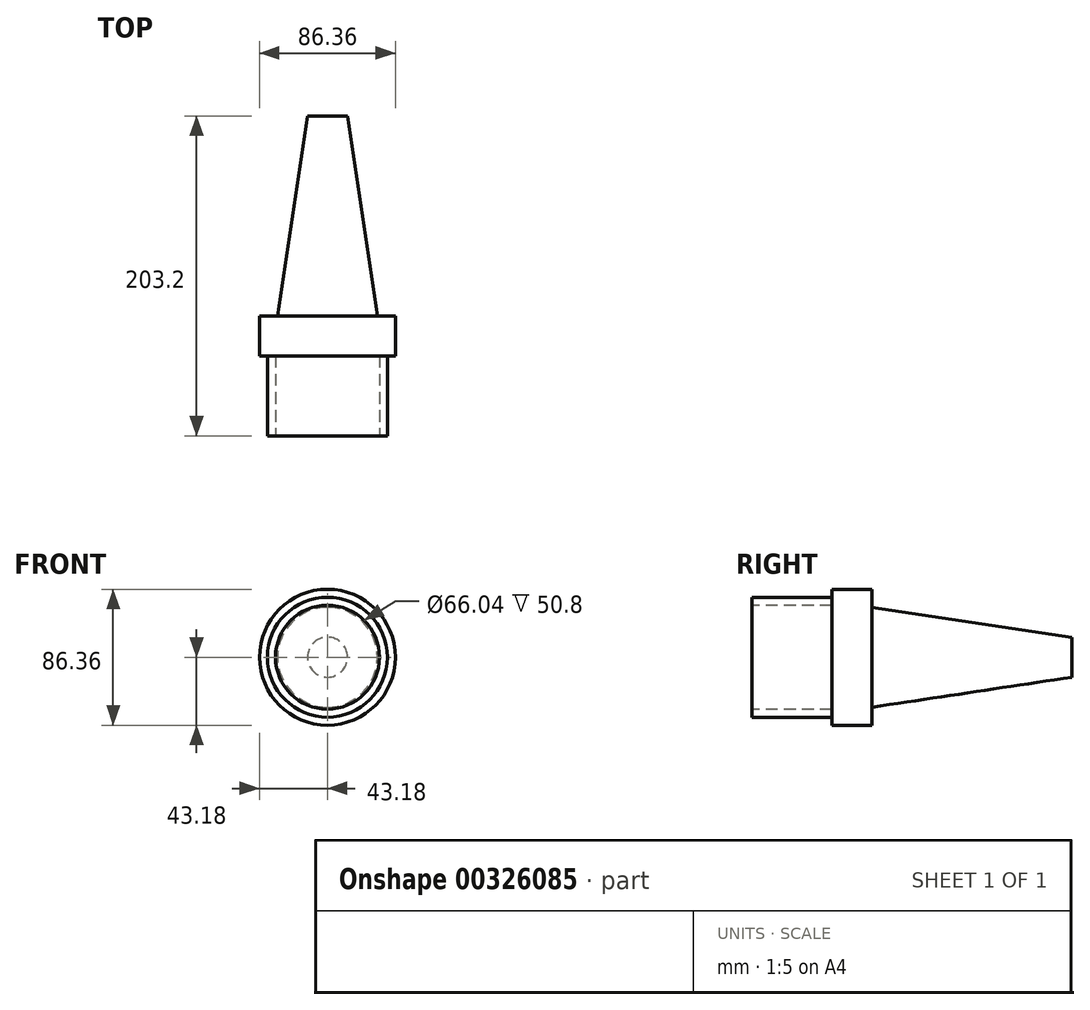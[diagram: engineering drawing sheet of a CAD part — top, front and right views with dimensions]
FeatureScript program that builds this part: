
annotation { "Feature Type Name" : "Feature", "Feature Type Description" : "" }
export const myFeature = defineFeature(function(context is Context, id is Id, definition is map)
    precondition{}
    {
        {
            var Q0;
            Q0=qCreatedBy(makeId("Front.planeOp"),FACE);
            var sketch = newSketch(context, id + "F0", { "sketchPlane" : qUnion([Q0])});
            skCircle(sketch, "E0", {"center": v(0, 0) * mm, "radius": 38.1 * mm});
            skSolve(sketch);
        }
        {
            var Q0;
            Q0 = qSketchRegion(id + "F0", true);
            extrude(context, id + "F1", {"entities" : qUnion([Q0]), "depth" : 76.2 * mm});
        }
        {
            var Q0;
            Q0=makeQuery(id+"F1.opExtrude","CAP_FACE",FACE,{"disambiguationData":[OSD([sQuery(id+"F0.wireOp",EDGE,"E0")])],"isStart":false});
            var sketch = newSketch(context, id + "F2", { "sketchPlane" : qUnion([Q0])});
            skCircle(sketch, "E1", {"center": v(0, 0) * mm, "radius": 33.02 * mm});
            skSolve(sketch);
        }
        {
            var Q0;
            Q0 = qSketchRegion(id + "F2", true);
            extrude(context, id + "F3", {"entities" : qUnion([Q0]), "operationType" : NewBodyOperationType.REMOVE, "oppositeDirection" : true, "depth" : 69.85 * mm});
        }
        {
            var Q0;
            Q0=makeQuery(id+"F1.opExtrude","CAP_FACE",FACE,{"disambiguationData":[OSD([sQuery(id+"F0.wireOp",EDGE,"E0")])],"isStart":true});
            var sketch = newSketch(context, id + "F4", { "sketchPlane" : qUnion([Q0])});
            skCircle(sketch, "E2", {"center": v(0, 0) * mm, "radius": 31.75 * mm});
            skSolve(sketch);
        }
        {
            var Q0;
            Q0=qCreatedBy(makeId("Front.planeOp"),FACE);
            var sketch = newSketch(context, id + "F5", { "sketchPlane" : qUnion([Q0])});
            skCircle(sketch, "E3", {"center": v(0, 0) * mm, "radius": 12.7 * mm});
            skSolve(sketch);
        }
        {
            var Q0;
            Q0=makeQuery(id+"F5.imprint","IMPRINT",FACE,{"disambiguationData":[TD([[makeQuery(id+"F5.imprint","IMPRINT",EDGE,{"derivedFrom":sQuery(id+"F5.wireOp",EDGE,"E3")}),1.0]])]});
            extrude(context, id + "F6", {"entities" : qUnion([Q0]), "operationType" : NewBodyOperationType.ADD, "oppositeDirection" : true, "depth" : 127 * mm});
        }
        {
            var Q1;
            Q1=makeQuery(id+"F6.opExtrude","CAP_FACE",FACE,{"disambiguationData":[OSD([sQuery(id+"F5.wireOp",EDGE,"E3")])],"isStart":false});
            var Q2;
            Q2=makeQuery(id+"F4.imprint","IMPRINT",FACE,{"disambiguationData":[TD([[makeQuery(id+"F4.imprint","IMPRINT",EDGE,{"derivedFrom":sQuery(id+"F4.wireOp",EDGE,"E2")}),1.0]])]});
            loft(context, id + "F7", {"operationType" : NewBodyOperationType.ADD, "sheetProfilesArray" : [{ "sheetProfileEntities" : qUnion([Q1]) }, { "sheetProfileEntities" : qUnion([Q2]) }]});
        }
        {
            var Q0;
            Q0=qCreatedBy(makeId("Front.planeOp"),FACE);
            var sketch = newSketch(context, id + "F8", { "sketchPlane" : qUnion([Q0])});
            skCircle(sketch, "E4", {"center": v(0, 0) * mm, "radius": 43.18 * mm});
            skSolve(sketch);
        }
        {
            var Q0;
            Q0=makeQuery(id+"F8.imprint","IMPRINT",FACE,{"disambiguationData":[TD([[makeQuery(id+"F8.imprint","IMPRINT",EDGE,{"derivedFrom":sQuery(id+"F8.wireOp",EDGE,"E4")}),1.0]])]});
            extrude(context, id + "F9", {"entities" : qUnion([Q0]), "operationType" : NewBodyOperationType.ADD, "depth" : 25.4 * mm});
        }
    });
